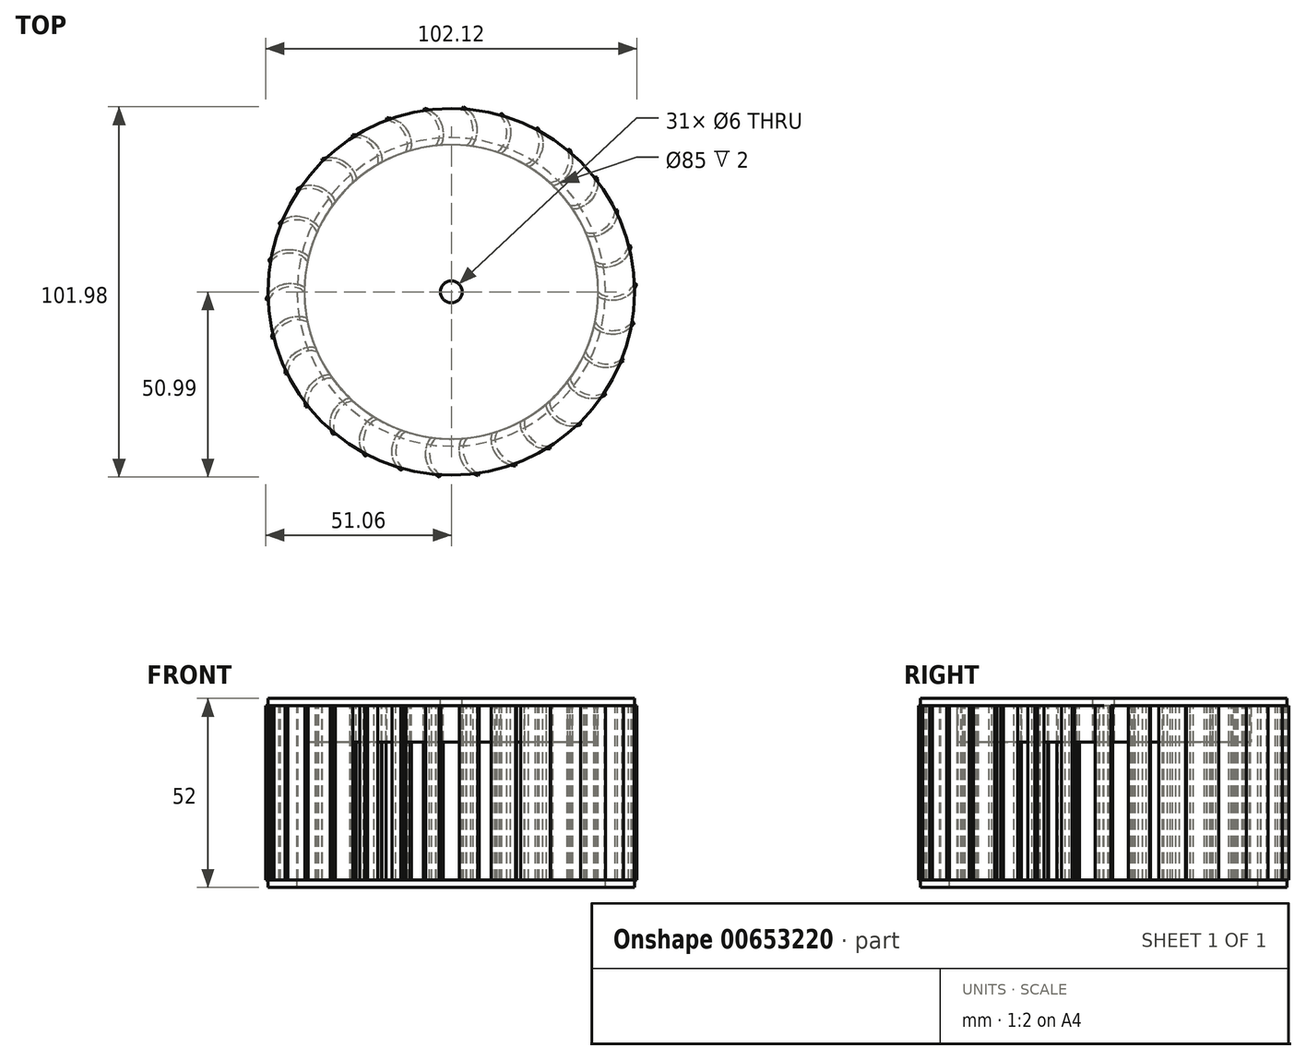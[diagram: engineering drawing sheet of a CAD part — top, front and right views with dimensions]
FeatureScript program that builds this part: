
annotation { "Feature Type Name" : "Feature", "Feature Type Description" : "" }
export const myFeature = defineFeature(function(context is Context, id is Id, definition is map)
    precondition{}
    {
        {
            var Q0;
            Q0=qCreatedBy(makeId("Top.planeOp"),FACE);
            var sketch = newSketch(context, id + "F0", { "sketchPlane" : qUnion([Q0])});
            skCircle(sketch, "E0", {"center": v(0, 0) * mm, "radius": 40.5 * mm});
            skSolve(sketch);
        }
        {
            var Q0;
            Q0=makeQuery(id+"F0.imprint","IMPRINT",FACE,{"disambiguationData":[TD([[makeQuery(id+"F0.imprint","IMPRINT",EDGE,{"derivedFrom":sQuery(id+"F0.wireOp",EDGE,"E0")}),1.0]])]});
            extrude(context, id + "F1", {"entities" : qUnion([Q0]), "depth" : 10 * mm, "offsetDistance" : 25 * mm});
        }
        {
            var Q0;
            Q0=makeQuery(id+"F1.opExtrude","CAP_FACE",FACE,{"disambiguationData":[OSD([sQuery(id+"F0.wireOp",EDGE,"E0")])],"isStart":false});
            var sketch = newSketch(context, id + "F2", { "sketchPlane" : qUnion([Q0])});
            skFitSpline(sketch, "E1", {"points": [v(20.2, 35.1) * mm, v(23.11, 44.9) * mm], "startDerivative": vector(10.47, 2.18) * mm, "endDerivative": vector(-7.52, 9.43) * mm});
            skFitSpline(sketch, "E2", {"points": [v(23.8, 45.21) * mm, v(21.24, 34.49) * mm], "startDerivative": vector(11.47, -15.62) * mm, "endDerivative": vector(-4.9, -0.12) * mm});
            skLineSegment(sketch, "E3", {"start": v(23.11, 44.9) * mm, "end": v(23.8, 45.21) * mm});
            skLineSegment(sketch, "E4", {"start": v(20.2, 35.1) * mm, "end": v(21.24, 34.49) * mm});
            skSolve(sketch);
        }
        {
            var Q0;
            {var subQ0=sQuery(id+"F2.wireOp",EDGE,"E1");Q0=makeQuery(id+"F2.imprint","IMPRINT",FACE,{"disambiguationData":[TD([[makeQuery(id+"F2.imprint","IMPRINT",EDGE,{"derivedFrom":subQ0}),-1.0]])]});}
            extrude(context, id + "F3", {"entities" : qUnion([Q0]), "operationType" : NewBodyOperationType.ADD, "oppositeDirection" : true, "depth" : 48 * mm, "offsetDistance" : 25 * mm});
        }
        {
            var Q0;
            Q0=makeQuery(id+"F1.opExtrude","CAP_FACE",FACE,{"disambiguationData":[OSD([sQuery(id+"F0.wireOp",EDGE,"E0")])],"isStart":true});
            var sketch = newSketch(context, id + "F4", { "sketchPlane" : qUnion([Q0])});
            skCircle(sketch, "E5", {"center": v(0, 0) * mm, "radius": 40 * mm});
            skSolve(sketch);
        }
        {
            var Q0;
            Q0=makeQuery(id+"F1.opExtrude","SWEPT_BODY",BODY,{"disambiguationData":[OSD([sQuery(id+"F0.wireOp",EDGE,"E0")])]});
            var Q1;
            Q1=makeQuery(id+"F1.opExtrude","SWEPT_FACE",FACE,{"disambiguationData":[OSD([sQuery(id+"F0.wireOp",EDGE,"E0")])]});
            circularPattern(context, id + "F5", {"entities" : qUnion([Q0]), "axis" : qUnion([Q1]), "angle" : 360 * degree, "instanceCount" : 30, "equalSpace" : true});
        }
        {
            var Q0;
            {var subQ0=sQuery(id+"F0.wireOp",EDGE,"E0");Q0=makeQuery(id+"F3.boolean.opBoolean","MERGE",FACE,{"derivedFrom":[makeQuery(id+"F1.opExtrude","CAP_FACE",FACE,{"disambiguationData":[OSD([subQ0])],"isStart":false}),makeQuery(id+"F3.opExtrude","CAP_FACE",FACE,{"disambiguationData":[OSD([subQ0,sQuery(id+"F2.wireOp",EDGE,"E1"),sQuery(id+"F2.wireOp",EDGE,"E2"),sQuery(id+"F2.wireOp",EDGE,"E3")])],"isStart":true})]});}
            var sketch = newSketch(context, id + "F6", { "sketchPlane" : qUnion([Q0])});
            skCircle(sketch, "E6", {"center": v(0, 0) * mm, "radius": 50.5 * mm});
            skSolve(sketch);
        }
        {
            var Q0;
            Q0=qSketchRegion(id+"F6",true);
            extrude(context, id + "F7", {"entities" : qUnion([Q0]), "depth" : 2 * mm, "offsetDistance" : 25 * mm});
        }
        {
            var Q0;
            Q0=makeQuery(id+"F5.opPattern","COPY",FACE,{"derivedFrom":makeQuery(id+"F3.opExtrude","CAP_FACE",FACE,{"disambiguationData":[OSD([sQuery(id+"F0.wireOp",EDGE,"E0"),sQuery(id+"F2.wireOp",EDGE,"E1"),sQuery(id+"F2.wireOp",EDGE,"E2"),sQuery(id+"F2.wireOp",EDGE,"E3")])],"isStart":false}),"instanceName":"15"});
            var sketch = newSketch(context, id + "F8", { "sketchPlane" : qUnion([Q0])});
            skCircle(sketch, "E7", {"center": v(0, 0) * mm, "radius": 50.5 * mm});
            skCircle(sketch, "E8", {"center": v(0, 0) * mm, "radius": 42.5 * mm});
            skSolve(sketch);
        }
        {
            var Q0;
            Q0=qSketchRegion(id+"F8",true);
            extrude(context, id + "F9", {"entities" : qUnion([Q0]), "depth" : 2 * mm, "offsetDistance" : 25 * mm});
        }
        {
            var Q0;
            Q0=makeQuery(id+"F7.opExtrude","CAP_FACE",FACE,{"disambiguationData":[OSD([sQuery(id+"F6.wireOp",EDGE,"E6")])],"isStart":false});
            var sketch = newSketch(context, id + "F10", { "sketchPlane" : qUnion([Q0])});
            skCircle(sketch, "E9", {"center": v(0, 0) * mm, "radius": 3 * mm});
            skSolve(sketch);
        }
        {
            var Q0;
            Q0=qSketchRegion(id+"F10",true);
            extrude(context, id + "F11", {"entities" : qUnion([Q0]), "operationType" : NewBodyOperationType.REMOVE, "endBound" : BoundingType.THROUGH_ALL, "oppositeDirection" : true, "depth" : 25 * mm, "offsetDistance" : 25 * mm});
        }
        {
            var Q0;
            Q0=makeQuery(id+"F4.imprint","IMPRINT",FACE,{"disambiguationData":[TD([[makeQuery(id+"F4.imprint","IMPRINT",EDGE,{"derivedFrom":sQuery(id+"F4.wireOp",EDGE,"E5")}),1.0]])]});
            var sketch = newSketch(context, id + "F12", { "sketchPlane" : qUnion([Q0])});
            skCircle(sketch, "E10", {"center": v(0, 0) * mm, "radius": 3 * mm});
            skSolve(sketch);
        }
        {
            var Q0;
            Q0=qSketchRegion(id+"F12",true);
            extrude(context, id + "F13", {"entities" : qUnion([Q0]), "operationType" : NewBodyOperationType.REMOVE, "oppositeDirection" : true, "depth" : 25 * mm, "offsetDistance" : 25 * mm});
        }
    });
